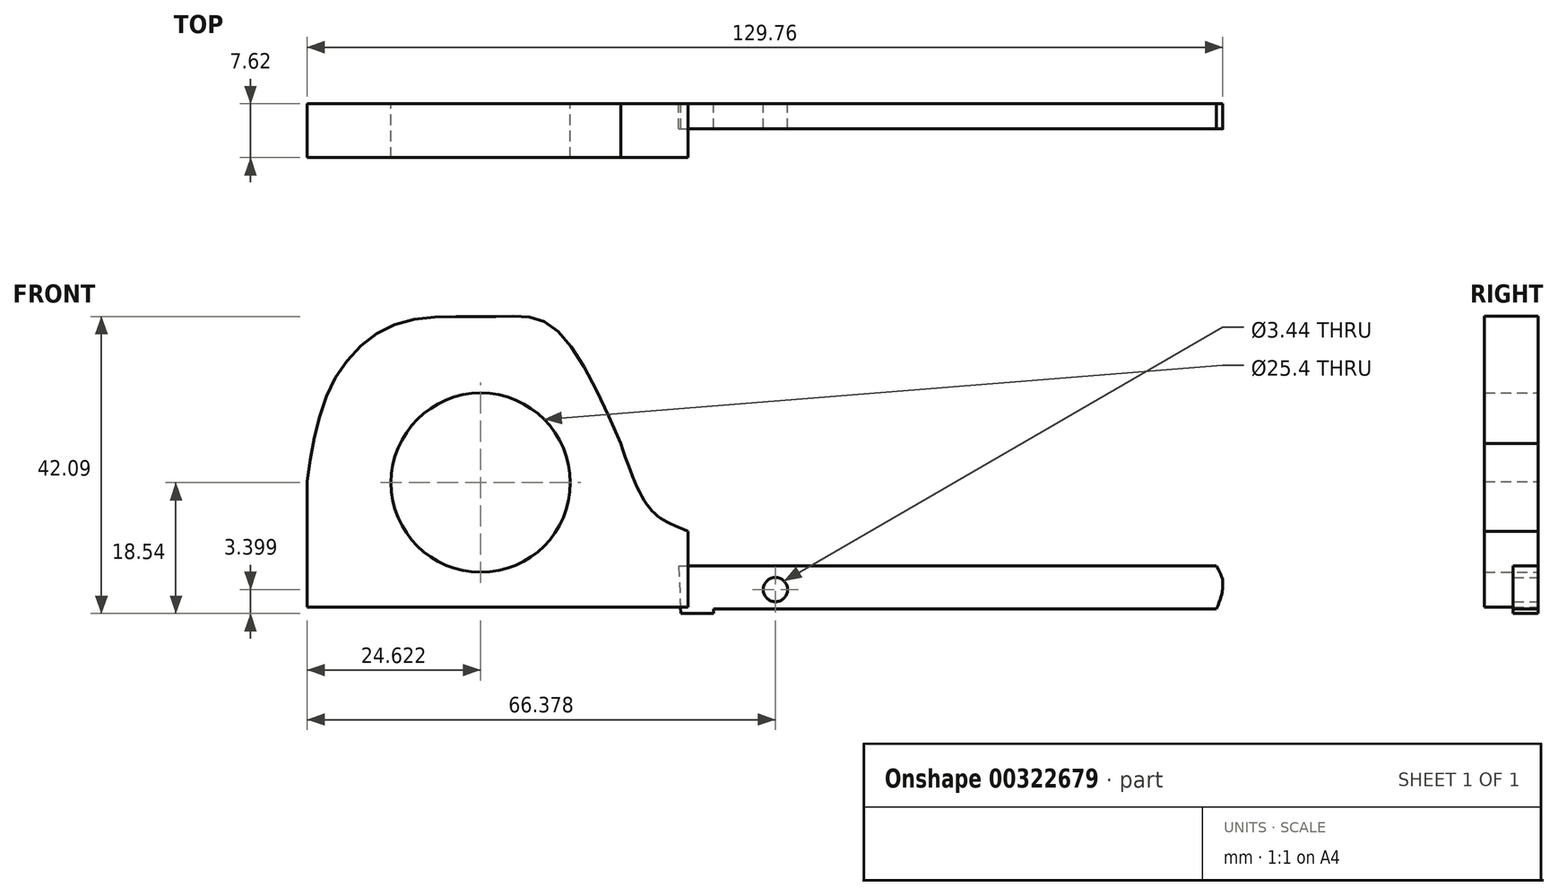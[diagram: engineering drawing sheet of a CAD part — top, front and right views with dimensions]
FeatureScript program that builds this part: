
annotation { "Feature Type Name" : "Feature", "Feature Type Description" : "" }
export const myFeature = defineFeature(function(context is Context, id is Id, definition is map)
    precondition{}
    {
        {
            var Q0;
            Q0=qCreatedBy(makeId("Front.planeOp"),FACE);
            var sketch = newSketch(context, id + "F0", { "sketchPlane" : qUnion([Q0])});
            skCircle(sketch, "E0", {"center": v(-49.88, 23.23) * mm, "radius": 12.7 * mm});
            skLineSegment(sketch, "E1", {"start": v(-74.5, 23.4) * mm, "end": v(-74.5, 5.61) * mm});
            skLineSegment(sketch, "E2", {"start": v(-74.5, 5.61) * mm, "end": v(-20.52, 5.61) * mm});
            skLineSegment(sketch, "E3", {"start": v(-20.52, 5.61) * mm, "end": v(-20.52, 16.34) * mm});
            skFitSpline(sketch, "E4", {"points": [v(-20.52, 16.34) * mm, v(-25.5, 19.12) * mm, v(-30.06, 28.8) * mm], "startDerivative": vector(-16.1, 7.32) * mm, "endDerivative": vector(-7.98, 23.78) * mm});
            skFitSpline(sketch, "E5", {"points": [v(-74.5, 23.4) * mm, v(-70.73, 37.65) * mm, v(-61.37, 45.84) * mm, v(-48.2, 46.72) * mm, v(-40.01, 45.55) * mm, v(-30.06, 28.8) * mm], "startDerivative": vector(11.02, 72.14) * mm, "endDerivative": vector(39.11, -88.84) * mm});
            skSolve(sketch);
        }
        {
            var Q0;
            Q0=makeQuery(id+"F0.imprint","IMPRINT",FACE,{"disambiguationData":[TD([[makeQuery(id+"F0.imprint","IMPRINT",EDGE,{"derivedFrom":sQuery(id+"F0.wireOp",EDGE,"E0")}),-1.0]])]});
            extrude(context, id + "F1", {"entities" : qUnion([Q0]), "depth" : 7.62 * mm});
        }
        {
            var Q0;
            Q0=qCreatedBy(makeId("Front.planeOp"),FACE);
            var sketch = newSketch(context, id + "F2", { "sketchPlane" : qUnion([Q0])});
            skLineSegment(sketch, "E6", {"start": v(-21.8, 11.42) * mm, "end": v(54.4, 11.42) * mm});
            skLineSegment(sketch, "E7", {"start": v(-21.55, 4.69) * mm, "end": v(-16.89, 4.69) * mm});
            skLineSegment(sketch, "E8", {"start": v(-16.89, 5.34) * mm, "end": v(-16.89, 4.69) * mm});
            skLineSegment(sketch, "E9", {"start": v(-16.89, 5.34) * mm, "end": v(54.4, 5.34) * mm});
            skFitSpline(sketch, "E10", {"points": [v(54.4, 11.42) * mm, v(55.25, 8.79) * mm, v(54.4, 5.34) * mm], "startDerivative": vector(6.21, -10.93) * mm, "endDerivative": vector(-5.23, -12.81) * mm});
            skCircle(sketch, "E11", {"center": v(-8.12, 8.09) * mm, "radius": 1.72 * mm});
            skLineSegment(sketch, "E12", {"start": v(-6.4, 8.1) * mm, "end": v(19.1, 8.1) * mm});
            skLineSegment(sketch, "E13", {"start": v(-21.8, 11.42) * mm, "end": v(-21.55, 4.69) * mm});
            skSolve(sketch);
        }
        {
            var Q0;
            Q0=makeQuery(id+"F2.imprint","IMPRINT",FACE,{"disambiguationData":[TD([[makeQuery(id+"F2.imprint","IMPRINT",EDGE,{"derivedFrom":sQuery(id+"F2.wireOp",EDGE,"E6")}),-1.0]])]});
            extrude(context, id + "F3", {"entities" : qUnion([Q0]), "depth" : 3.56 * mm});
        }
    });
